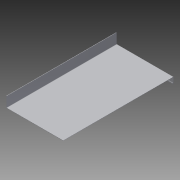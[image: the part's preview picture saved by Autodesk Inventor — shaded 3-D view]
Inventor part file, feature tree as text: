
AUTODESK INVENTOR PART (.ipt)
format: ipt  version: 2013 (Build 170138000, 138)  size: 144,896 bytes
history: native  units: in
note: dims shown in document units (in); Inventor stores cm internally (conversion verified against a paired STEP export)
features: sheet_metal_op x8, sketch x4, other x4
ambient origin geometry x8: Origin, YZ Plane, XZ Plane, XY Plane, X Axis, Y Axis, Z Axis, Center Point
bodies: Solid1 (feature_tree)
feature tree (16):
  sheet_metal_op  "Face1"
  sheet_metal_op  "Flange1"
  sheet_metal_op  "Hem1"
  sheet_metal_op  "Flange2"
  sketch  "Sketch1"  dims[d0=21.5in]
  other  "Plate1"
  sketch  "Sketch2"  dims[d1=42.0in]
  other  "Plate2"
  sheet_metal_op  "Bend1"
  sheet_metal_op  "Corner1"
  sketch  "Sketch4"  dims[d3=0.12in d4=0.06in d5=0.24in d6=0.12in d7=2.5in d8=90.0deg d9=0.12in d10=0.48in d11=0.12in d12=0.12in d13=0.12in d14=0.06in d15=0.24in d16=0.12in d17=0.48in d18=0.06in d19=0.03in d20=0.12in d21=0.06in d22=0.24in d23=0.12in d24=4.0in d25=90.0deg d26=0.12in d27=0.48in d28=0.12in d29=0.12in]
  other  "Plate3"
  sheet_metal_op  "Bend2"
  sheet_metal_op  "Corner2"
  sketch  "Sketch3"  dims[d2=0.12in]
  other  "Definition1"
